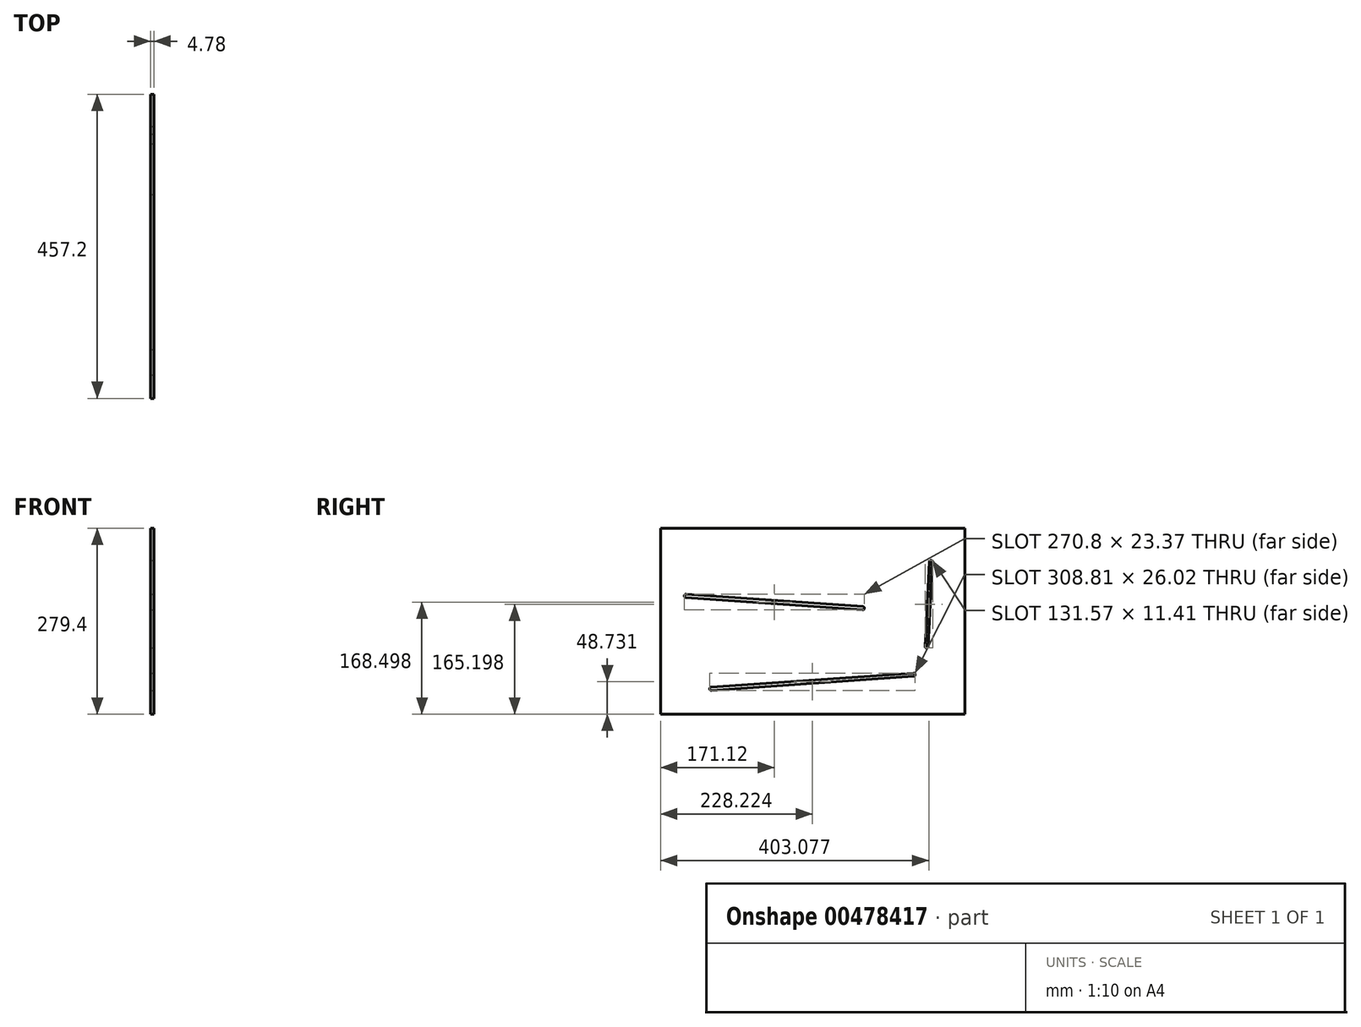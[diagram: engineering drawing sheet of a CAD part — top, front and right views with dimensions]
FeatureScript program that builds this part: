
annotation { "Feature Type Name" : "Feature", "Feature Type Description" : "" }
export const myFeature = defineFeature(function(context is Context, id is Id, definition is map)
    precondition{}
    {
        {
            var Q0;
            Q0=qCreatedBy(makeId("Right.planeOp"),FACE);
            var sketch = newSketch(context, id + "F0", { "sketchPlane" : qUnion([Q0])});
            skLineSegment(sketch, "E0.bottom", {"start": v(0, 0) * mm, "end": v(457.2, 0) * mm});
            skLineSegment(sketch, "E0.top", {"start": v(0, 279.4) * mm, "end": v(457.2, 279.4) * mm});
            skLineSegment(sketch, "E0.left", {"start": v(0, 0) * mm, "end": v(0, 279.4) * mm});
            skLineSegment(sketch, "E0.right", {"start": v(457.2, 0) * mm, "end": v(457.2, 279.4) * mm});
            skSolve(sketch);
        }
        {
            var Q0;
            Q0=qSketchRegion(id+"F0",true);
            extrude(context, id + "F1", {"entities" : qUnion([Q0]), "depth" : 4.78 * mm});
        }
        {
            var Q0;
            Q0=makeQuery(id+"F1.opExtrude","CAP_FACE",FACE,{"disambiguationData":[OSD([sQuery(id+"F0.wireOp",EDGE,"E0.bottom"),sQuery(id+"F0.wireOp",EDGE,"E0.top"),sQuery(id+"F0.wireOp",EDGE,"E0.left"),sQuery(id+"F0.wireOp",EDGE,"E0.right")])],"isStart":false});
            var sketch = newSketch(context, id + "F2", { "sketchPlane" : qUnion([Q0])});
            skLineSegment(sketch, "E1", {"start": v(25.43, 178.69) * mm, "end": v(316.8, 158.31) * mm, "construction": true});
            skArc(sketch, "E2", {"start": v(38.27, 180.18) * mm, "mid": v(35.72, 177.97) * mm, "end": v(37.93, 175.42) * mm});
            skArc(sketch, "E3", {"start": v(303.97, 156.81) * mm, "mid": v(306.52, 159.03) * mm, "end": v(304.3, 161.58) * mm});
            skLineSegment(sketch, "E4", {"start": v(38.27, 180.18) * mm, "end": v(304.3, 161.58) * mm});
            skLineSegment(sketch, "E5", {"start": v(37.93, 175.42) * mm, "end": v(303.97, 156.81) * mm});
            skSolve(sketch);
        }
        {
            var Q0;
            Q0=makeQuery(id+"F2.imprint","IMPRINT",FACE,{"disambiguationData":[TD([[makeQuery(id+"F2.imprint","IMPRINT",EDGE,{"derivedFrom":sQuery(id+"F2.wireOp",EDGE,"E2")}),-1.0]])]});
            var sketch = newSketch(context, id + "F3", { "sketchPlane" : qUnion([Q0])});
            skLineSegment(sketch, "E6", {"start": v(63.53, 37.21) * mm, "end": v(392.92, 60.25) * mm, "construction": true});
            skArc(sketch, "E7", {"start": v(76.03, 40.48) * mm, "mid": v(73.82, 37.93) * mm, "end": v(76.37, 35.72) * mm});
            skArc(sketch, "E8", {"start": v(380.41, 56.98) * mm, "mid": v(382.63, 59.53) * mm, "end": v(380.08, 61.74) * mm});
            skLineSegment(sketch, "E9", {"start": v(76.03, 40.48) * mm, "end": v(380.08, 61.74) * mm});
            skLineSegment(sketch, "E10", {"start": v(76.37, 35.72) * mm, "end": v(380.41, 56.98) * mm});
            skSolve(sketch);
        }
        {
            var Q0;
            Q0=makeQuery(id+"F2.imprint","IMPRINT",FACE,{"disambiguationData":[TD([[makeQuery(id+"F2.imprint","IMPRINT",EDGE,{"derivedFrom":sQuery(id+"F2.wireOp",EDGE,"E2")}),-1.0]])]});
            var sketch = newSketch(context, id + "F4", { "sketchPlane" : qUnion([Q0])});
            skLineSegment(sketch, "E11", {"start": v(407.06, 241.28) * mm, "end": v(399.09, 89.11) * mm, "construction": true});
            skArc(sketch, "E12", {"start": v(408.78, 228.48) * mm, "mid": v(406.52, 230.98) * mm, "end": v(404.02, 228.72) * mm});
            skArc(sketch, "E13", {"start": v(397.37, 101.92) * mm, "mid": v(399.63, 99.41) * mm, "end": v(402.14, 101.67) * mm});
            skLineSegment(sketch, "E14", {"start": v(408.78, 228.48) * mm, "end": v(402.14, 101.67) * mm});
            skLineSegment(sketch, "E15", {"start": v(404.02, 228.72) * mm, "end": v(397.37, 101.92) * mm});
            skSolve(sketch);
        }
        {
            var Q0;
            Q0 = qSketchRegion(id + "F4", true);
            var Q1;
            Q1 = qSketchRegion(id + "F3", true);
            var Q2;
            Q2 = qSketchRegion(id + "F2", true);
            extrude(context, id + "F5", {"entities" : qUnion([Q0, Q1, Q2]), "operationType" : NewBodyOperationType.REMOVE, "endBound" : BoundingType.THROUGH_ALL, "oppositeDirection" : true, "depth" : 25.4 * mm});
        }
    });
